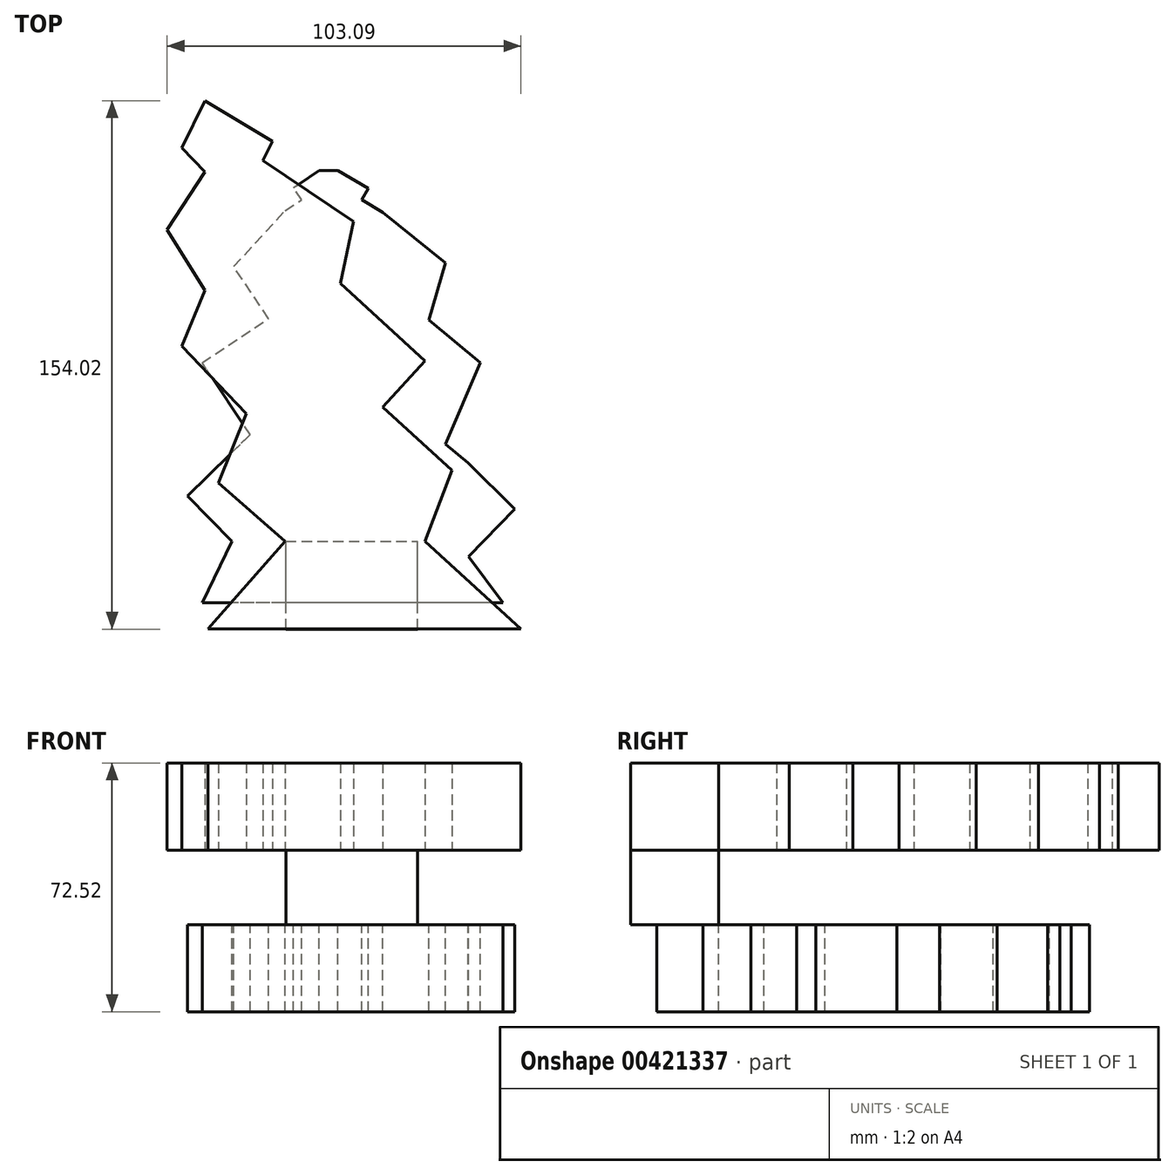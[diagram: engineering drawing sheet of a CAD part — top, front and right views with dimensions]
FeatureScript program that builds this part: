
annotation { "Feature Type Name" : "Feature", "Feature Type Description" : "" }
export const myFeature = defineFeature(function(context is Context, id is Id, definition is map)
    precondition{}
    {
        {
            var Q0;
            Q0=qCreatedBy(makeId("Front.planeOp"),FACE);
            var sketch = newSketch(context, id + "F0", { "sketchPlane" : qUnion([Q0])});
            skLineSegment(sketch, "E0.bottom", {"start": v(-28.2, 0) * mm, "end": v(10.22, 0) * mm});
            skLineSegment(sketch, "E0.top", {"start": v(-28.2, -21.72) * mm, "end": v(10.22, -21.72) * mm});
            skLineSegment(sketch, "E0.left", {"start": v(-28.2, 0) * mm, "end": v(-28.2, -21.72) * mm});
            skLineSegment(sketch, "E0.right", {"start": v(10.22, 0) * mm, "end": v(10.22, -21.72) * mm});
            skLineSegment(sketch, "E1.bottom", {"start": v(10.22, -21.72) * mm, "end": v(37.17, -21.72) * mm});
            skLineSegment(sketch, "E1.top", {"start": v(10.22, -21.72) * mm, "end": v(37.17, -21.72) * mm});
            skLineSegment(sketch, "E1.left", {"start": v(10.22, -21.72) * mm, "end": v(10.22, -21.72) * mm});
            skLineSegment(sketch, "E1.right", {"start": v(37.17, -21.72) * mm, "end": v(37.17, -21.72) * mm});
            skLineSegment(sketch, "E2.bottom", {"start": v(37.17, -11.08) * mm, "end": v(37.17, -11.08) * mm});
            skLineSegment(sketch, "E2.top", {"start": v(37.17, 0) * mm, "end": v(37.17, 0) * mm});
            skLineSegment(sketch, "E2.left", {"start": v(37.17, -11.08) * mm, "end": v(37.17, 0) * mm});
            skLineSegment(sketch, "E2.right", {"start": v(37.17, -11.08) * mm, "end": v(37.17, 0) * mm});
            skLineSegment(sketch, "E3.bottom", {"start": v(10.22, 0) * mm, "end": v(37.17, 0) * mm});
            skLineSegment(sketch, "E3.top", {"start": v(10.22, 0) * mm, "end": v(37.17, 0) * mm});
            skLineSegment(sketch, "E3.left", {"start": v(10.22, 0) * mm, "end": v(10.22, 0) * mm});
            skLineSegment(sketch, "E4.top", {"start": v(37.17, -19.42) * mm, "end": v(37.17, -19.42) * mm});
            skLineSegment(sketch, "E4.left", {"start": v(37.17, -11.08) * mm, "end": v(37.17, -19.42) * mm});
            skLineSegment(sketch, "E4.right", {"start": v(37.17, -11.08) * mm, "end": v(37.17, -19.42) * mm});
            skSolve(sketch);
        }
        {
            var Q0;
            Q0=makeQuery(id+"F0.imprint","IMPRINT",FACE,{"disambiguationData":[TD([[makeQuery(id+"F0.imprint","IMPRINT",EDGE,{"derivedFrom":sQuery(id+"F0.wireOp",EDGE,"E0.bottom")}),-1.0]])]});
            extrude(context, id + "F1", {"entities" : qUnion([Q0]), "depth" : 25.65 * mm});
        }
        {
            var Q0;
            Q0=qCreatedBy(makeId("Top.planeOp"),FACE);
            var sketch = newSketch(context, id + "F2", { "sketchPlane" : qUnion([Q0])});
            skLineSegment(sketch, "E5", {"start": v(12.34, 0) * mm, "end": v(40.29, -25.6) * mm});
            skLineSegment(sketch, "E6", {"start": v(40.29, -25.6) * mm, "end": v(12.03, -25.6) * mm});
            skLineSegment(sketch, "E7", {"start": v(12.03, -25.6) * mm, "end": v(-50.9, -25.6) * mm});
            skLineSegment(sketch, "E8", {"start": v(-50.9, -25.6) * mm, "end": v(-28.47, 0) * mm});
            skLineSegment(sketch, "E9", {"start": v(-28.47, 0) * mm, "end": v(-47.82, 16.95) * mm});
            skLineSegment(sketch, "E10", {"start": v(-47.82, 16.95) * mm, "end": v(-39.72, 37.18) * mm});
            skLineSegment(sketch, "E11", {"start": v(-39.72, 37.18) * mm, "end": v(-58.52, 56.87) * mm});
            skLineSegment(sketch, "E12", {"start": v(12.34, 0) * mm, "end": v(20.21, 20.6) * mm});
            skLineSegment(sketch, "E13", {"start": v(20.21, 20.6) * mm, "end": v(0, 39.12) * mm});
            skLineSegment(sketch, "E14", {"start": v(0, 39.12) * mm, "end": v(12.34, 52.58) * mm});
            skLineSegment(sketch, "E15", {"start": v(12.34, 52.58) * mm, "end": v(-12.25, 75.1) * mm});
            skLineSegment(sketch, "E16", {"start": v(-12.25, 75.1) * mm, "end": v(-8.49, 93.2) * mm});
            skLineSegment(sketch, "E17", {"start": v(-8.49, 93.2) * mm, "end": v(-34.86, 110.99) * mm});
            skLineSegment(sketch, "E18", {"start": v(-58.52, 56.87) * mm, "end": v(-51.81, 73.13) * mm});
            skLineSegment(sketch, "E19", {"start": v(-51.81, 73.13) * mm, "end": v(-62.8, 90.73) * mm});
            skLineSegment(sketch, "E20", {"start": v(-62.8, 90.73) * mm, "end": v(-51.81, 107.62) * mm});
            skLineSegment(sketch, "E21", {"start": v(-51.81, 107.62) * mm, "end": v(-58.52, 114.65) * mm});
            skLineSegment(sketch, "E22", {"start": v(-58.52, 114.65) * mm, "end": v(-51.81, 128.37) * mm});
            skLineSegment(sketch, "E23", {"start": v(-34.86, 110.99) * mm, "end": v(-32.16, 116.51) * mm});
            skLineSegment(sketch, "E24", {"start": v(-32.16, 116.51) * mm, "end": v(-51.81, 128.37) * mm});
            skSolve(sketch);
        }
        {
            var Q0;
            Q0=makeQuery(id+"F2.imprint","IMPRINT",FACE,{"disambiguationData":[TD([[makeQuery(id+"F2.imprint","IMPRINT",EDGE,{"derivedFrom":sQuery(id+"F2.wireOp",EDGE,"E5")}),-1.0]])]});
            extrude(context, id + "F3", {"entities" : qUnion([Q0]), "operationType" : NewBodyOperationType.ADD, "depth" : 25.4 * mm});
        }
        {
            var Q0;
            Q0=makeQuery(id+"F1.opExtrude","SWEPT_FACE",FACE,{"disambiguationData":[OSD([sQuery(id+"F0.wireOp",EDGE,"E0.top")])]});
            var sketch = newSketch(context, id + "F4", { "sketchPlane" : qUnion([Q0])});
            skLineSegment(sketch, "E25", {"start": v(-28.2, 25.65) * mm, "end": v(-28.2, 18) * mm});
            skLineSegment(sketch, "E26", {"start": v(-28.2, 18) * mm, "end": v(-52.57, 18) * mm});
            skLineSegment(sketch, "E27", {"start": v(-52.57, 18) * mm, "end": v(-43.94, 0) * mm});
            skLineSegment(sketch, "E28", {"start": v(-43.94, 0) * mm, "end": v(-56.84, -13.17) * mm});
            skLineSegment(sketch, "E29", {"start": v(-56.84, -13.17) * mm, "end": v(-38.62, -31) * mm});
            skLineSegment(sketch, "E30", {"start": v(-38.62, -31) * mm, "end": v(-52.57, -52) * mm});
            skLineSegment(sketch, "E31", {"start": v(-52.57, -52) * mm, "end": v(-33.27, -64.83) * mm});
            skLineSegment(sketch, "E32", {"start": v(-28.2, 18) * mm, "end": v(35.07, 18) * mm});
            skLineSegment(sketch, "E33", {"start": v(35.07, 18) * mm, "end": v(24.99, 4.5) * mm});
            skLineSegment(sketch, "E34", {"start": v(24.99, 4.5) * mm, "end": v(38.56, -9.36) * mm});
            skLineSegment(sketch, "E35", {"start": v(38.56, -9.36) * mm, "end": v(24.88, -22.75) * mm});
            skLineSegment(sketch, "E36", {"start": v(24.88, -22.75) * mm, "end": v(18.28, -28.3) * mm});
            skLineSegment(sketch, "E37", {"start": v(18.28, -28.3) * mm, "end": v(28.5, -52) * mm});
            skLineSegment(sketch, "E38", {"start": v(28.5, -52) * mm, "end": v(13.43, -64.43) * mm});
            skLineSegment(sketch, "E39", {"start": v(13.43, -64.43) * mm, "end": v(18.28, -81.1) * mm});
            skLineSegment(sketch, "E40", {"start": v(-33.27, -64.83) * mm, "end": v(-43.39, -80.04) * mm});
            skLineSegment(sketch, "E41", {"start": v(-43.39, -80.04) * mm, "end": v(-28.35, -96.35) * mm});
            skLineSegment(sketch, "E42", {"start": v(-28.35, -96.35) * mm, "end": v(-23.64, -99.48) * mm});
            skLineSegment(sketch, "E43", {"start": v(18.28, -81.1) * mm, "end": v(0, -95.87) * mm});
            skLineSegment(sketch, "E44", {"start": v(0, -95.87) * mm, "end": v(-6.1, -99.47) * mm});
            skLineSegment(sketch, "E45", {"start": v(-6.1, -99.47) * mm, "end": v(-4.15, -102.77) * mm});
            skLineSegment(sketch, "E46", {"start": v(-4.15, -102.77) * mm, "end": v(-13.07, -108.03) * mm});
            skLineSegment(sketch, "E47", {"start": v(-23.64, -99.48) * mm, "end": v(-26, -103.02) * mm});
            skPoint(sketch, "E47.endSnap0", {"position": v(-26, -97.91) * mm});
            skLineSegment(sketch, "E48", {"start": v(-26, -103.02) * mm, "end": v(-18.46, -108.03) * mm});
            skLineSegment(sketch, "E49", {"start": v(-18.46, -108.03) * mm, "end": v(-13.07, -108.03) * mm});
            skSolve(sketch);
        }
        {
            var Q0;
            Q0 = qSketchRegion(id + "F4", true);
            extrude(context, id + "F5", {"entities" : qUnion([Q0]), "operationType" : NewBodyOperationType.ADD, "depth" : 25.4 * mm});
        }
    });
